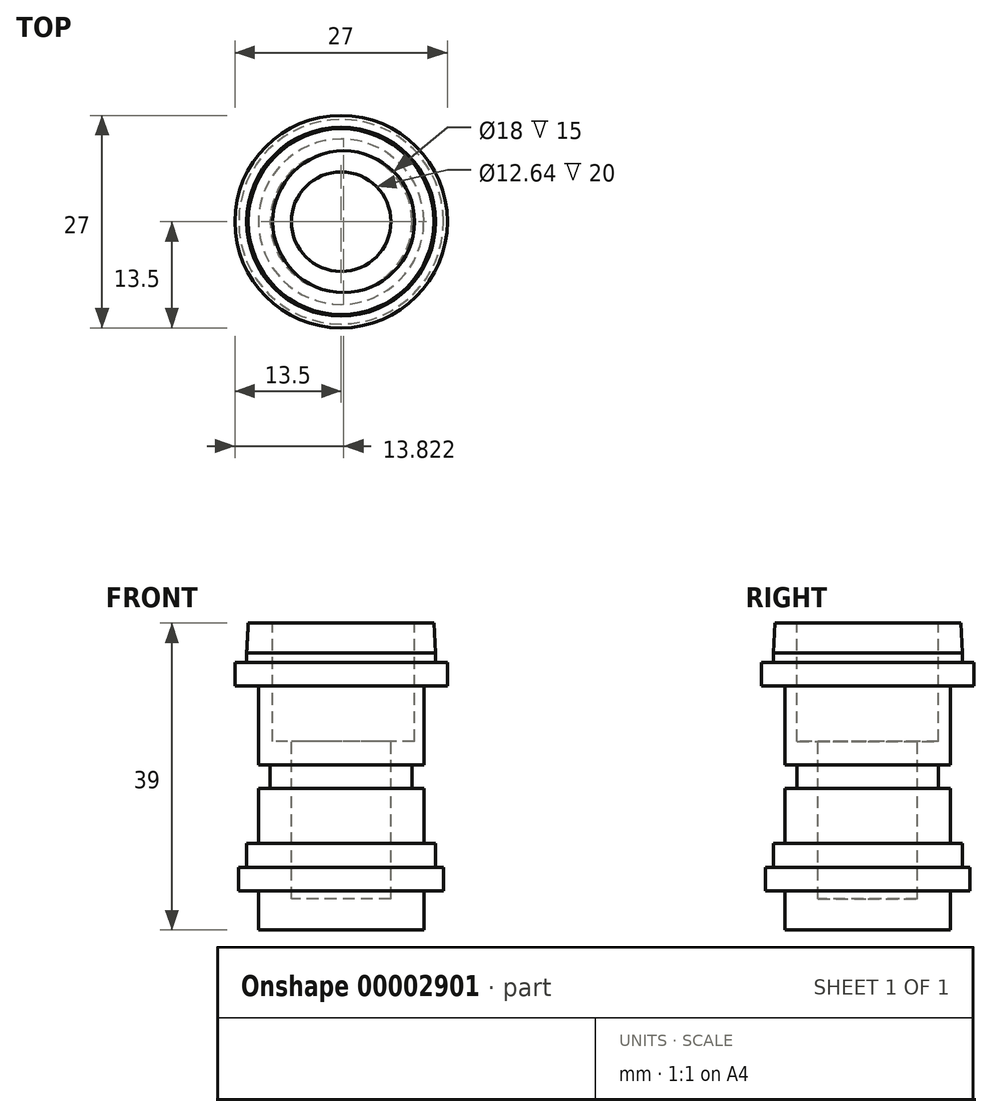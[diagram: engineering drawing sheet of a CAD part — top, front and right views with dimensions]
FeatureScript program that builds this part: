
annotation { "Feature Type Name" : "Feature", "Feature Type Description" : "" }
export const myFeature = defineFeature(function(context is Context, id is Id, definition is map)
    precondition{}
    {
        {
            var Q0;
            Q0=qCreatedBy(makeId("Front.planeOp"),FACE);
            cPlane(context, id + "F0", {"entities" : qUnion([Q0]), "cplaneType" : CPlaneType.OFFSET, "offset" : 0 * mm, "width" : 150 * mm, "height" : 150 * mm});
        }
        {
            var Q0;
            Q0=qCreatedBy(id+"F0.planeOp",FACE);
            var sketch = newSketch(context, id + "F1", { "sketchPlane" : qUnion([Q0])});
            skLineSegment(sketch, "E0", {"start": v(0, 0) * mm, "end": v(-10.5, 0) * mm});
            skLineSegment(sketch, "E1", {"start": v(-10.5, 0) * mm, "end": v(-10.5, 5) * mm});
            skLineSegment(sketch, "E2", {"start": v(-10.5, 5) * mm, "end": v(-13, 5) * mm});
            skLineSegment(sketch, "E3", {"start": v(-13, 5) * mm, "end": v(-13, 8) * mm});
            skLineSegment(sketch, "E4", {"start": v(-13, 8) * mm, "end": v(-12, 8) * mm});
            skLineSegment(sketch, "E5", {"start": v(-12, 8) * mm, "end": v(-12, 11) * mm});
            skLineSegment(sketch, "E6", {"start": v(-12, 11) * mm, "end": v(-10.5, 11) * mm});
            skLineSegment(sketch, "E7", {"start": v(-10.5, 11) * mm, "end": v(-10.5, 18) * mm});
            skLineSegment(sketch, "E8", {"start": v(-10.5, 18) * mm, "end": v(-9, 18) * mm});
            skLineSegment(sketch, "E9", {"start": v(-9, 18) * mm, "end": v(-9, 21) * mm});
            skLineSegment(sketch, "E10", {"start": v(-9, 21) * mm, "end": v(-10.5, 21) * mm});
            skLineSegment(sketch, "E11", {"start": v(-10.5, 21) * mm, "end": v(-10.5, 31) * mm});
            skLineSegment(sketch, "E12", {"start": v(-10.5, 31) * mm, "end": v(-13.5, 31) * mm});
            skLineSegment(sketch, "E13", {"start": v(-13.5, 31) * mm, "end": v(-13.5, 34) * mm});
            skLineSegment(sketch, "E14", {"start": v(-13.5, 34) * mm, "end": v(-12, 34) * mm});
            skLineSegment(sketch, "E15", {"start": v(-12, 34) * mm, "end": v(-12, 39) * mm});
            skLineSegment(sketch, "E16", {"start": v(-12, 39) * mm, "end": v(0, 39) * mm});
            skLineSegment(sketch, "E17", {"start": v(0, 39) * mm, "end": v(0, 0) * mm});
            skLineSegment(sketch, "E18", {"start": v(-11.86, 0) * mm, "end": v(0, 0) * mm, "construction": true});
            skLineSegment(sketch, "E19", {"start": v(-12, 45.68) * mm, "end": v(-12, 0) * mm, "construction": true});
            skLineSegment(sketch, "E20", {"start": v(-13.5, 45.68) * mm, "end": v(-13.5, 0) * mm, "construction": true});
            skLineSegment(sketch, "E21", {"start": v(-9, 45.68) * mm, "end": v(-9, 0) * mm, "construction": true});
            skLineSegment(sketch, "E22", {"start": v(-13, 45.68) * mm, "end": v(-13, 0) * mm, "construction": true});
            skLineSegment(sketch, "E23", {"start": v(0, 45.68) * mm, "end": v(0, 0) * mm, "construction": true});
            skLineSegment(sketch, "E24", {"start": v(-10.5, 45.68) * mm, "end": v(-10.5, 0) * mm, "construction": true});
            skLineSegment(sketch, "E25", {"start": v(0, 45.68) * mm, "end": v(-9, 45.68) * mm, "construction": true});
            skLineSegment(sketch, "E26", {"start": v(-9, 45.68) * mm, "end": v(-10.5, 45.68) * mm, "construction": true});
            skLineSegment(sketch, "E27", {"start": v(-10.5, 45.68) * mm, "end": v(-12, 45.68) * mm, "construction": true});
            skLineSegment(sketch, "E28", {"start": v(-12, 45.68) * mm, "end": v(-13, 45.68) * mm, "construction": true});
            skLineSegment(sketch, "E29", {"start": v(-13.5, 45.68) * mm, "end": v(-13, 45.68) * mm, "construction": true});
            skSolve(sketch);
        }
        {
            var Q0;
            Q0=makeQuery(id+"F1.imprint","IMPRINT",FACE,{"disambiguationData":[TD([[makeQuery(id+"F1.imprint","IMPRINT",EDGE,{"derivedFrom":sQuery(id+"F1.wireOp",EDGE,"E0")}),-1.0]])]});
            var Q1;
            Q1=sQuery(id+"F1.wireOp",EDGE,"E17");
            revolve(context, id + "F2", {"entities" : qUnion([Q0]), "axis" : qUnion([Q1]), "revolveType" : RevolveType.FULL});
        }
        {
            var Q0;
            Q0=makeQuery(id+"F2.opRevolve","SWEPT_FACE",FACE,{"disambiguationData":[OSD([sQuery(id+"F1.wireOp",EDGE,"E16")])]});
            var sketch = newSketch(context, id + "F3", { "sketchPlane" : qUnion([Q0])});
            skCircle(sketch, "E30", {"center": v(0, 0) * mm, "radius": 6.32 * mm});
            skLineSegment(sketch, "E31", {"start": v(0.32, 0) * mm, "end": v(6.32, 0) * mm, "construction": true});
            skCircle(sketch, "E32", {"center": v(0.32, 0) * mm, "radius": 9 * mm});
            skLineSegment(sketch, "E33", {"start": v(0.32, 0) * mm, "end": v(0.32, -9) * mm, "construction": true});
            skSolve(sketch);
        }
        {
            var Q0;
            Q0=makeQuery(id+"F3.imprint","IMPRINT",FACE,{"disambiguationData":[TD([[makeQuery(id+"F3.imprint","IMPRINT",EDGE,{"derivedFrom":sQuery(id+"F3.wireOp",EDGE,"E30")}),1.0]])]});
            extrude(context, id + "F4", {"entities" : qUnion([Q0]), "operationType" : NewBodyOperationType.REMOVE, "oppositeDirection" : true, "depth" : 35 * mm});
        }
        {
            var Q0;
            Q0=makeQuery(id+"F3.imprint","IMPRINT",FACE,{"disambiguationData":[TD([[makeQuery(id+"F3.imprint","IMPRINT",EDGE,{"derivedFrom":sQuery(id+"F3.wireOp",EDGE,"E30")}),-1.0]])]});
            extrude(context, id + "F5", {"entities" : qUnion([Q0]), "operationType" : NewBodyOperationType.REMOVE, "oppositeDirection" : true, "depth" : 15 * mm});
        }
        {
            var Q0;
            Q0=makeQuery(id+"F2.opRevolve","SWEPT_EDGE",EDGE,{"disambiguationData":[OSD([sQuery(id+"F1.wireOp",EDGE,"E15"),sQuery(id+"F1.wireOp",EDGE,"E16")])]});
            chamfer(context, id + "F6", {"entities" : qUnion([Q0]), "chamferType" : ChamferType.OFFSET_ANGLE, "width" : .2 * mm, "oppositeDirection" : false, "angle" : 87 * degree, "tangentPropagation" : true});
        }
    });
